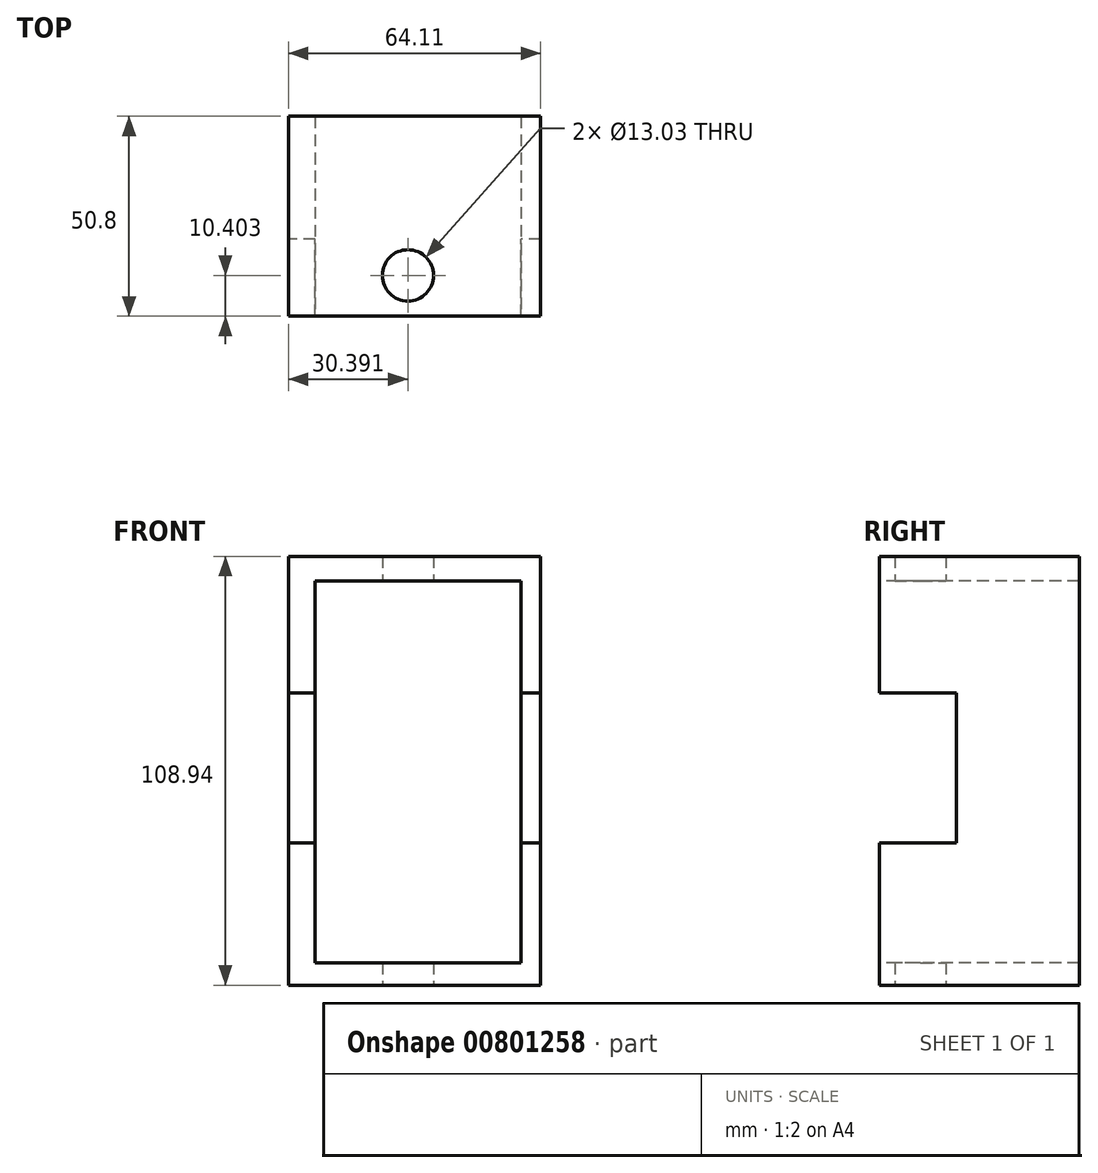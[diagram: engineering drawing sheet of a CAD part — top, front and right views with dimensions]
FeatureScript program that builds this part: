
annotation { "Feature Type Name" : "Feature", "Feature Type Description" : "" }
export const myFeature = defineFeature(function(context is Context, id is Id, definition is map)
    precondition{}
    {
        {
            var Q0;
            Q0=qCreatedBy(makeId("Front.planeOp"),FACE);
            var sketch = newSketch(context, id + "F0", { "sketchPlane" : qUnion([Q0])});
            skLineSegment(sketch, "E0", {"start": v(-37.92, 44.96) * mm, "end": v(26.2, 44.96) * mm});
            skLineSegment(sketch, "E1", {"start": v(26.2, 44.96) * mm, "end": v(26.2, -63.98) * mm});
            skLineSegment(sketch, "E2", {"start": v(26.2, -63.98) * mm, "end": v(-37.92, -63.98) * mm});
            skLineSegment(sketch, "E3", {"start": v(-37.92, -63.98) * mm, "end": v(-37.92, 44.96) * mm});
            skSolve(sketch);
        }
        {
            var Q0;
            Q0=makeQuery(id+"F0.imprint","IMPRINT",FACE,{"disambiguationData":[TD([[makeQuery(id+"F0.imprint","IMPRINT",EDGE,{"derivedFrom":sQuery(id+"F0.wireOp",EDGE,"E0")}),-1.0]])]});
            extrude(context, id + "F1", {"entities" : qUnion([Q0]), "depth" : 50.8 * mm, "offsetDistance" : 25.4 * mm});
        }
        {
            var Q0;
            Q0=makeQuery(id+"F1.opExtrude","SWEPT_FACE",FACE,{"disambiguationData":[OSD([sQuery(id+"F0.wireOp",EDGE,"E3")])]});
            var sketch = newSketch(context, id + "F2", { "sketchPlane" : qUnion([Q0])});
            skLineSegment(sketch, "E4", {"start": v(50.8, 10.27) * mm, "end": v(31.2, 10.27) * mm});
            skLineSegment(sketch, "E5", {"start": v(31.2, 10.27) * mm, "end": v(31.2, -27.89) * mm});
            skLineSegment(sketch, "E6", {"start": v(31.2, -27.89) * mm, "end": v(50.8, -27.89) * mm});
            skSolve(sketch);
        }
        {
            var Q0;
            Q0=makeQuery(id+"F1.opExtrude","CAP_FACE",FACE,{"disambiguationData":[OSD([sQuery(id+"F0.wireOp",EDGE,"E0"),sQuery(id+"F0.wireOp",EDGE,"E1"),sQuery(id+"F0.wireOp",EDGE,"E2"),sQuery(id+"F0.wireOp",EDGE,"E3")])],"isStart":false});
            var sketch = newSketch(context, id + "F3", { "sketchPlane" : qUnion([Q0])});
            skLineSegment(sketch, "E7.bottom", {"start": v(21.17, 38.73) * mm, "end": v(-31.07, 38.73) * mm});
            skLineSegment(sketch, "E7.top", {"start": v(21.17, -58.25) * mm, "end": v(-31.07, -58.25) * mm});
            skLineSegment(sketch, "E7.left", {"start": v(21.17, 38.73) * mm, "end": v(21.17, -58.25) * mm});
            skLineSegment(sketch, "E7.right", {"start": v(-31.07, 38.73) * mm, "end": v(-31.07, -58.25) * mm});
            skSolve(sketch);
        }
        {
            var Q0;
            Q0=makeQuery(id+"F3.imprint","IMPRINT",FACE,{"disambiguationData":[TD([[makeQuery(id+"F3.imprint","IMPRINT",EDGE,{"derivedFrom":sQuery(id+"F3.wireOp",EDGE,"E7.bottom")}),1.0]])]});
            extrude(context, id + "F4", {"entities" : qUnion([Q0]), "operationType" : NewBodyOperationType.REMOVE, "oppositeDirection" : true, "depth" : 131.32 * mm, "offsetDistance" : 25.4 * mm});
        }
        {
            var Q0;
            {var subQ0=sQuery(id+"F2.wireOp",EDGE,"E4");Q0=makeQuery(id+"F2.imprint","IMPRINT",FACE,{"disambiguationData":[TD([[makeQuery(id+"F2.imprint","IMPRINT",EDGE,{"derivedFrom":subQ0}),1.0]])]});}
            extrude(context, id + "F5", {"entities" : qUnion([Q0]), "operationType" : NewBodyOperationType.REMOVE, "oppositeDirection" : true, "depth" : 116.08 * mm, "offsetDistance" : 25.4 * mm});
        }
        {
            var Q0;
            Q0=makeQuery(id+"F1.opExtrude","SWEPT_FACE",FACE,{"disambiguationData":[OSD([sQuery(id+"F0.wireOp",EDGE,"E2")])]});
            var sketch = newSketch(context, id + "F6", { "sketchPlane" : qUnion([Q0])});
            skCircle(sketch, "E8", {"center": v(-7.53, 40.4) * mm, "radius": 6.51 * mm});
            skSolve(sketch);
        }
        {
            var Q0;
            Q0=makeQuery(id+"F6.imprint","IMPRINT",FACE,{"disambiguationData":[TD([[makeQuery(id+"F6.imprint","IMPRINT",EDGE,{"derivedFrom":sQuery(id+"F6.wireOp",EDGE,"E8")}),1.0]])]});
            extrude(context, id + "F7", {"entities" : qUnion([Q0]), "operationType" : NewBodyOperationType.REMOVE, "oppositeDirection" : true, "depth" : 143.5 * mm, "offsetDistance" : 25.4 * mm});
        }
    });
